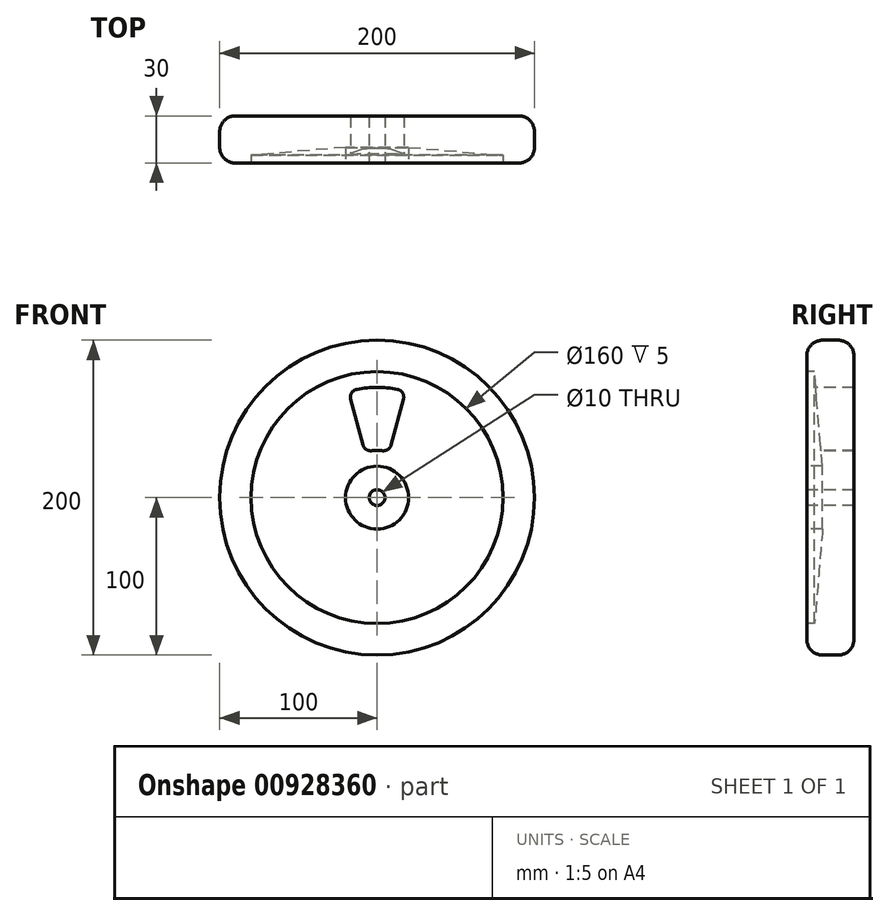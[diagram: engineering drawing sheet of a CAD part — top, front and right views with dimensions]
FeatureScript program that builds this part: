
annotation { "Feature Type Name" : "Feature", "Feature Type Description" : "" }
export const myFeature = defineFeature(function(context is Context, id is Id, definition is map)
    precondition{}
    {
        {
            var Q0;
            Q0=qCreatedBy(makeId("Front.planeOp"),FACE);
            var sketch = newSketch(context, id + "F0", { "sketchPlane" : qUnion([Q0])});
            skCircle(sketch, "E0", {"center": v(0, 0) * mm, "radius": 100 * mm});
            skSolve(sketch);
        }
        {
            var Q0;
            Q0 = qSketchRegion(id + "F0", true);
            extrude(context, id + "F1", {"entities" : qUnion([Q0]), "depth" : 15 * mm, "offsetDistance" : 25 * mm, "hasSecondDirection" : true, "secondDirectionOppositeDirection" : true, "secondDirectionDepth" : 15 * mm});
        }
        {
            var Q0;
            Q0=makeQuery(id+"F1.opExtrude","CAP_EDGE",EDGE,{"disambiguationData":[OSD([sQuery(id+"F0.wireOp",EDGE,"E0")])],"isStart":false});
            var Q1;
            Q1=makeQuery(id+"F1.opExtrude","CAP_EDGE",EDGE,{"disambiguationData":[OSD([sQuery(id+"F0.wireOp",EDGE,"E0")])],"isStart":true});
            fillet(context, id + "F2", {"entities" : qUnion([Q0, Q1]), "radius" : 10 * mm, "tangentPropagation" : true, "allowEdgeOverflow" : false});
        }
        {
            var Q0;
            Q0=qCreatedBy(makeId("Right.planeOp"),FACE);
            var sketch = newSketch(context, id + "F3", { "sketchPlane" : qUnion([Q0])});
            skLineSegment(sketch, "E1.0", {"start": v(5, -100) * mm, "end": v(5, 100) * mm, "construction": true});
            skLineSegment(sketch, "E1.1", {"start": v(-5, 100) * mm, "end": v(-5, -100) * mm, "construction": true});
            skLineSegment(sketch, "E2", {"start": v(-5, 100) * mm, "end": v(5, 100) * mm, "construction": true});
            skLineSegment(sketch, "E3", {"start": v(-5, -100) * mm, "end": v(5, -100) * mm, "construction": true});
            skPoint(sketch, "E4", {"position": v(-5, 0) * mm});
            skLineSegment(sketch, "E5", {"start": v(-5, 20) * mm, "end": v(-5, -20) * mm});
            skLineSegment(sketch, "E6", {"start": v(-5, 100) * mm, "end": v(-5, 80) * mm});
            skLineSegment(sketch, "E7.0", {"start": v(-15, -90) * mm, "end": v(-15, 90) * mm, "construction": true});
            skLineSegment(sketch, "E8", {"start": v(-5, 80) * mm, "end": v(-15, 80) * mm, "construction": true});
            skLineSegment(sketch, "E9", {"start": v(-10, 80) * mm, "end": v(-15, 80) * mm});
            skLineSegment(sketch, "E10", {"start": v(-10, 80) * mm, "end": v(-5, 20) * mm});
            skLineSegment(sketch, "E11", {"start": v(-5, 20) * mm, "end": v(-15, 20) * mm});
            skLineSegment(sketch, "E12", {"start": v(-15, 20) * mm, "end": v(-15, 80) * mm});
            skSolve(sketch);
        }
        {
            var Q0;
            Q0=qCreatedBy(makeId("Right.planeOp"),FACE);
            var sketch = newSketch(context, id + "F4", { "sketchPlane" : qUnion([Q0])});
            skLineSegment(sketch, "E13", {"start": v(60, 0) * mm, "end": v(-60, 0) * mm});
            skSolve(sketch);
        }
        {
            var Q0;
            Q0 = qSketchRegion(id + "F3", true);
            var Q1;
            Q1=sQuery(id+"F4.wireOp",EDGE,"E13");
            revolve(context, id + "F5", {"operationType" : NewBodyOperationType.REMOVE, "surfaceOperationType" : NewSurfaceOperationType.NEW, "entities" : qUnion([Q0]), "axis" : qUnion([Q1]), "revolveType" : RevolveType.FULL, "oppositeDirection" : true});
        }
        {
            var Q0;
            Q0=qCreatedBy(makeId("Front.planeOp"),FACE);
            var sketch = newSketch(context, id + "F6", { "sketchPlane" : qUnion([Q0])});
            skCircle(sketch, "E14.0", {"center": v(0, 0) * mm, "radius": 100 * mm, "construction": true});
            skLineSegment(sketch, "E15", {"start": v(0, 0) * mm, "end": v(0, 100) * mm, "construction": true});
            skCircle(sketch, "E16.0", {"center": v(0, 0) * mm, "radius": 20 * mm, "construction": true});
            skCircle(sketch, "E17.0", {"center": v(0, 0) * mm, "radius": 30 * mm, "construction": true});
            skCircle(sketch, "E18.0", {"center": v(0, 0) * mm, "radius": 80 * mm, "construction": true});
            skCircle(sketch, "E19.0", {"center": v(0, 0) * mm, "radius": 70 * mm, "construction": true});
            skArc(sketch, "E20", {"start": v(3.55, 29.79) * mm, "mid": v(0, 30) * mm, "end": v(-3.55, 29.79) * mm});
            skLineSegment(sketch, "E21", {"start": v(0, 0) * mm, "end": v(18.12, 67.61) * mm, "construction": true});
            skLineSegment(sketch, "E22", {"start": v(0, 0) * mm, "end": v(-25.88, 96.6) * mm, "construction": true});
            skArc(sketch, "E23", {"start": v(12.86, 68.8) * mm, "mid": v(0, 70) * mm, "end": v(-12.86, 68.8) * mm});
            skLineSegment(sketch, "E24", {"start": v(8.97, 33.46) * mm, "end": v(16.77, 62.6) * mm});
            skLineSegment(sketch, "E25", {"start": v(-8.97, 33.46) * mm, "end": v(-16.77, 62.6) * mm});
            skPoint(sketch, "E26.visualSharp", {"position": v(-18.12, 67.61) * mm});
            skArc(sketch, "E26.filletArc", {"start": v(-12.86, 68.8) * mm, "mid": v(-16.17, 66.56) * mm, "end": v(-16.77, 62.6) * mm});
            skPoint(sketch, "E27.visualSharp", {"position": v(18.12, 67.61) * mm});
            skArc(sketch, "E27.filletArc", {"start": v(16.77, 62.6) * mm, "mid": v(16.17, 66.56) * mm, "end": v(12.86, 68.8) * mm});
            skPoint(sketch, "E28.visualSharp", {"position": v(7.76, 28.98) * mm});
            skArc(sketch, "E28.filletArc", {"start": v(3.55, 29.79) * mm, "mid": v(6.94, 30.61) * mm, "end": v(8.97, 33.46) * mm});
            skPoint(sketch, "E29.visualSharp", {"position": v(-7.76, 28.98) * mm});
            skArc(sketch, "E29.filletArc", {"start": v(-8.97, 33.46) * mm, "mid": v(-6.94, 30.61) * mm, "end": v(-3.55, 29.79) * mm});
            skSolve(sketch);
        }
        {
            var Q0;
            Q0 = qSketchRegion(id + "F6", true);
            extrude(context, id + "F7", {"entities" : qUnion([Q0]), "operationType" : NewBodyOperationType.REMOVE, "endBound" : BoundingType.THROUGH_ALL, "oppositeDirection" : true, "depth" : 25 * mm, "offsetDistance" : 25 * mm, "hasSecondDirection" : true, "secondDirectionBound" : SecondDirectionBoundingType.THROUGH_ALL, "secondDirectionOppositeDirection" : false, "secondDirectionDepth" : 25 * mm});
        }
        {
            var Q0;
            Q0=makeQuery(id+"F5.boolean.opBoolean","SPLIT",FACE,{"disambiguationData":[TD([makeQuery(id+"F5.opRevolve","SWEPT_FACE",FACE,{"disambiguationData":[OSD([sQuery(id+"F3.wireOp",EDGE,"E11")])]})])],"derivedFrom":makeQuery(id+"F1.opExtrude","CAP_FACE",FACE,{"disambiguationData":[OSD([sQuery(id+"F0.wireOp",EDGE,"E0")])],"isStart":false})});
            var sketch = newSketch(context, id + "F8", { "sketchPlane" : qUnion([Q0])});
            skCircle(sketch, "E30", {"center": v(0, 0) * mm, "radius": 5 * mm});
            skSolve(sketch);
        }
        {
            var Q0;
            Q0 = qSketchRegion(id + "F8", true);
            extrude(context, id + "F9", {"entities" : qUnion([Q0]), "operationType" : NewBodyOperationType.REMOVE, "endBound" : BoundingType.THROUGH_ALL, "oppositeDirection" : true, "depth" : 25 * mm, "offsetDistance" : 25 * mm});
        }
    });
